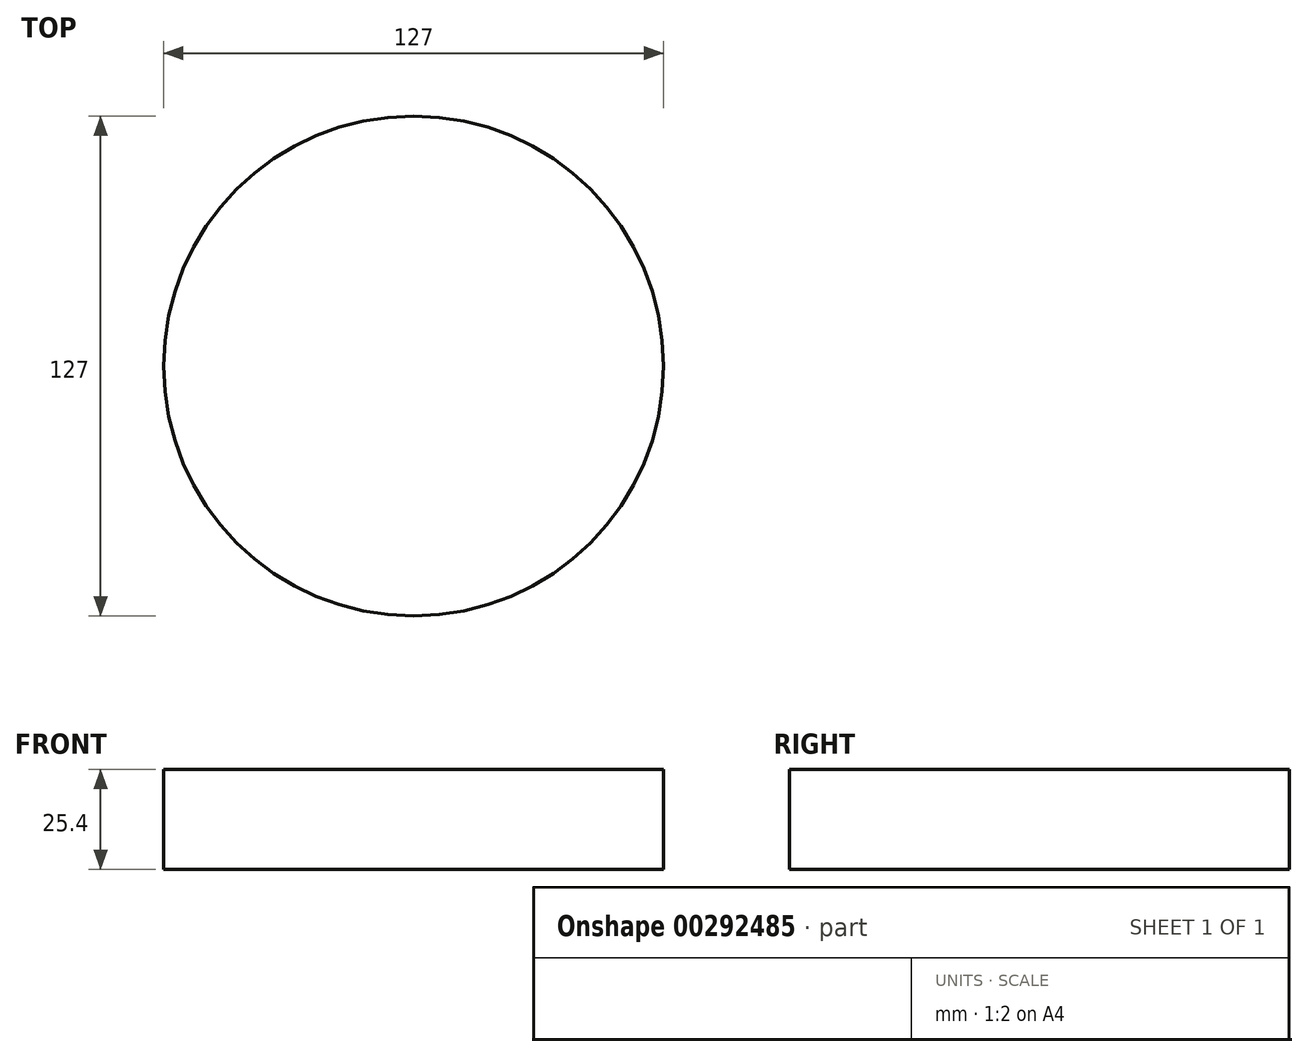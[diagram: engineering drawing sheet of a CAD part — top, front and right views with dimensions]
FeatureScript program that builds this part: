
annotation { "Feature Type Name" : "Feature", "Feature Type Description" : "" }
export const myFeature = defineFeature(function(context is Context, id is Id, definition is map)
    precondition{}
    {
        {
            var Q0;
            Q0=qCreatedBy(makeId("Top.planeOp"),FACE);
            var sketch = newSketch(context, id + "F0", { "sketchPlane" : qUnion([Q0])});
            skCircle(sketch, "E0", {"center": v(62.22, -23.05) * mm, "radius": 63.5 * mm});
            skSolve(sketch);
        }
        {
            var Q0;
            Q0=makeQuery(id+"F0.imprint","IMPRINT",FACE,{"disambiguationData":[TD([[makeQuery(id+"F0.imprint","IMPRINT",EDGE,{"derivedFrom":sQuery(id+"F0.wireOp",EDGE,"E0")}),1.0]])]});
            extrude(context, id + "F1", {"entities" : qUnion([Q0]), "depth" : 25.4 * mm});
        }
    });
